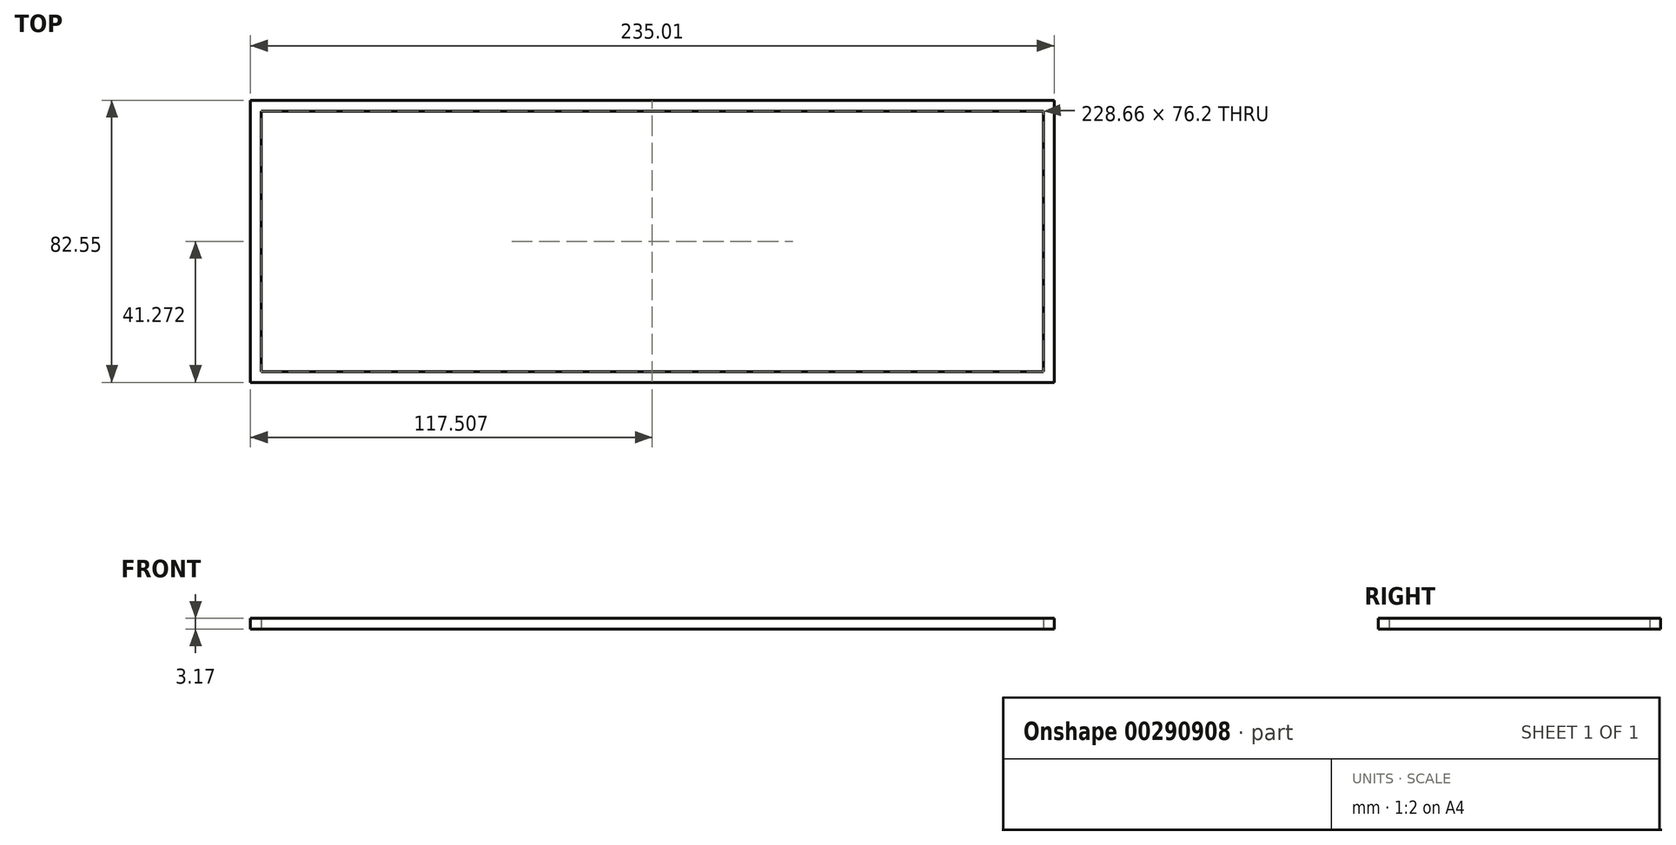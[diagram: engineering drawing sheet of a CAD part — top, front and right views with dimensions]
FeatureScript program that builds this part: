
annotation { "Feature Type Name" : "Feature", "Feature Type Description" : "" }
export const myFeature = defineFeature(function(context is Context, id is Id, definition is map)
    precondition{}
    {
        {
            var Q0;
            Q0=qCreatedBy(makeId("Top.planeOp"),FACE);
            var sketch = newSketch(context, id + "F0", { "sketchPlane" : qUnion([Q0])});
            skLineSegment(sketch, "E0.bottom", {"start": v(-117.29, 42) * mm, "end": v(117.72, 42) * mm});
            skLineSegment(sketch, "E0.top", {"start": v(-117.29, -40.54) * mm, "end": v(117.72, -40.54) * mm});
            skLineSegment(sketch, "E0.left", {"start": v(-117.29, 42) * mm, "end": v(-117.29, -40.54) * mm});
            skLineSegment(sketch, "E0.right", {"start": v(117.72, 42) * mm, "end": v(117.72, -40.54) * mm});
            skLineSegment(sketch, "E1.0", {"start": v(114.55, 38.83) * mm, "end": v(114.55, -37.37) * mm});
            skLineSegment(sketch, "E1.1", {"start": v(-114.11, 38.83) * mm, "end": v(114.55, 38.83) * mm});
            skLineSegment(sketch, "E1.2", {"start": v(-114.11, 38.83) * mm, "end": v(-114.11, -37.37) * mm});
            skLineSegment(sketch, "E1.3", {"start": v(-114.11, -37.37) * mm, "end": v(114.55, -37.37) * mm});
            skLineSegment(sketch, "E2", {"start": v(0.22, 42) * mm, "end": v(0.22, -40.54) * mm, "construction": true});
            skSolve(sketch);
        }
        {
            var Q0;
            Q0=makeQuery(id+"F0.imprint","IMPRINT",FACE,{"disambiguationData":[TD([[makeQuery(id+"F0.imprint","IMPRINT",EDGE,{"derivedFrom":sQuery(id+"F0.wireOp",EDGE,"E0.bottom")}),-1.0]])]});
            extrude(context, id + "F1", {"entities" : qUnion([Q0]), "depth" : 3.17 * mm});
        }
    });
